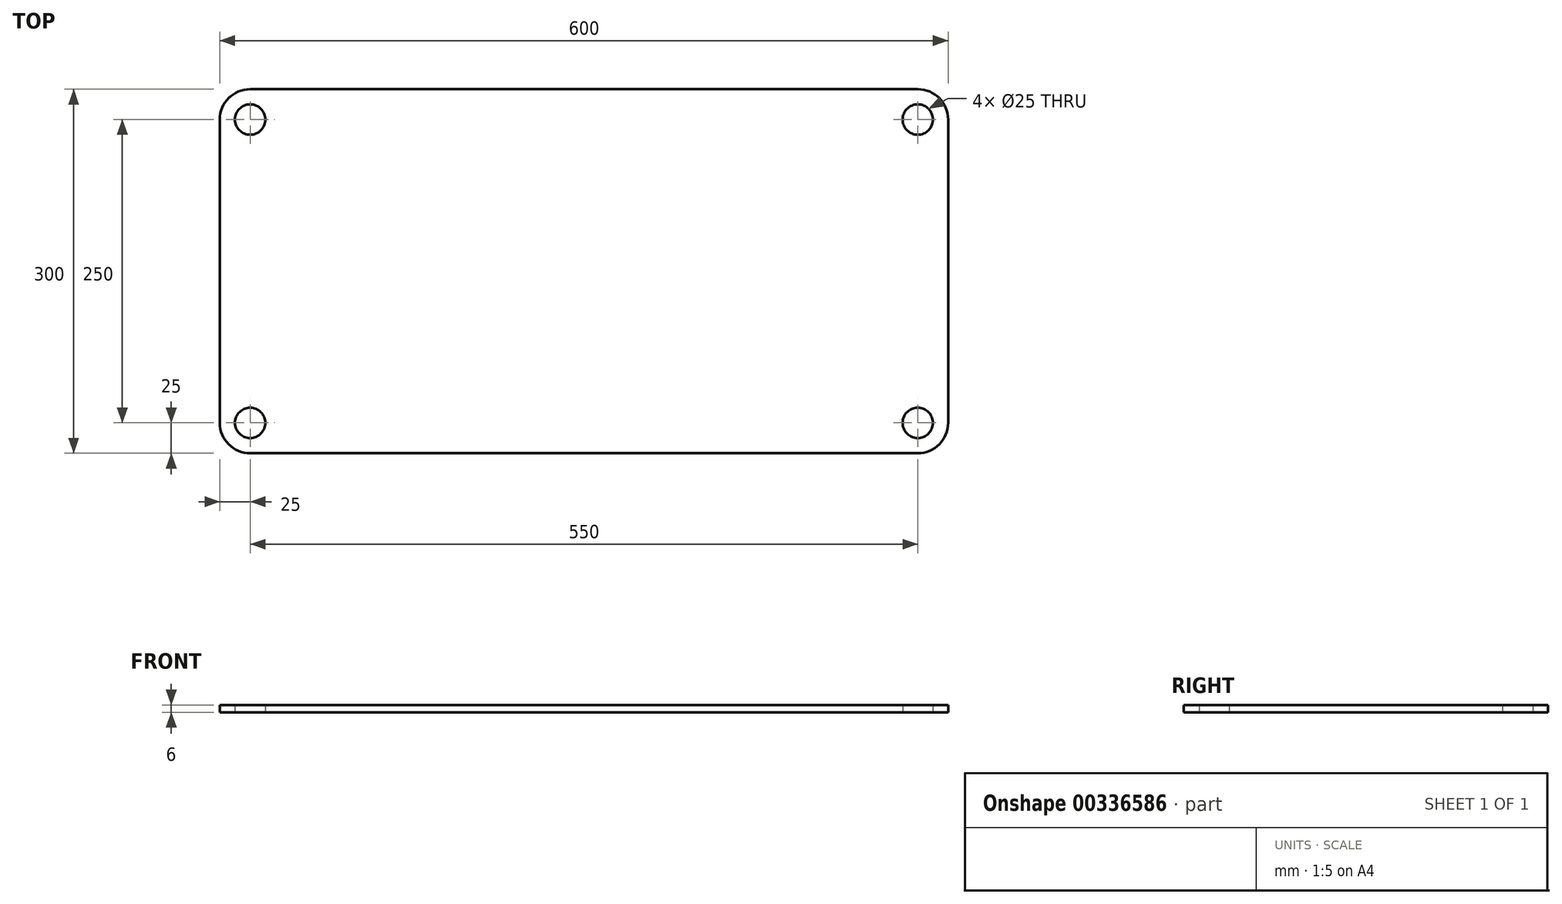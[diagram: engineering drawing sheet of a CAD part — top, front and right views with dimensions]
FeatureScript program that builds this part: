
annotation { "Feature Type Name" : "Feature", "Feature Type Description" : "" }
export const myFeature = defineFeature(function(context is Context, id is Id, definition is map)
    precondition{}
    {
        {
            var Q0;
            Q0=qCreatedBy(makeId("Top.planeOp"),FACE);
            var sketch = newSketch(context, id + "F0", { "sketchPlane" : qUnion([Q0])});
            skLineSegment(sketch, "E0.bottom", {"start": v(275, -150) * mm, "end": v(-275, -150) * mm});
            skLineSegment(sketch, "E0.top", {"start": v(275, 150) * mm, "end": v(-275, 150) * mm});
            skLineSegment(sketch, "E0.left", {"start": v(300, -125) * mm, "end": v(300, 125) * mm});
            skLineSegment(sketch, "E0.right", {"start": v(-300, -125) * mm, "end": v(-300, 125) * mm});
            skPoint(sketch, "E0.middle", {"position": v(0, 0) * mm});
            skPoint(sketch, "E1.visualSharp", {"position": v(-300, 150) * mm});
            skArc(sketch, "E1.filletArc", {"start": v(-275, 150) * mm, "mid": v(-292.68, 142.68) * mm, "end": v(-300, 125) * mm});
            skPoint(sketch, "E2.visualSharp", {"position": v(-300, -150) * mm});
            skArc(sketch, "E2.filletArc", {"start": v(-300, -125) * mm, "mid": v(-292.68, -142.68) * mm, "end": v(-275, -150) * mm});
            skPoint(sketch, "E3.visualSharp", {"position": v(300, 150) * mm});
            skArc(sketch, "E3.filletArc", {"start": v(300, 125) * mm, "mid": v(292.68, 142.68) * mm, "end": v(275, 150) * mm});
            skPoint(sketch, "E4.visualSharp", {"position": v(300, -150) * mm});
            skArc(sketch, "E4.filletArc", {"start": v(275, -150) * mm, "mid": v(292.68, -142.68) * mm, "end": v(300, -125) * mm});
            skSolve(sketch);
        }
        {
            var Q0;
            Q0=makeQuery(id+"F0.imprint","IMPRINT",FACE,{"disambiguationData":[TD([[makeQuery(id+"F0.imprint","IMPRINT",EDGE,{"derivedFrom":sQuery(id+"F0.wireOp",EDGE,"E0.bottom")}),-1.0]])]});
            extrude(context, id + "F1", {"entities" : qUnion([Q0]), "depth" : 6 * mm});
        }
        {
            var Q0;
            Q0=sQuery(id+"F0.wireOp",VERTEX,"E2.filletArc.center");
            var Q1;
            Q1=makeQuery(id+"F1.opExtrude","SWEPT_BODY",BODY,{"disambiguationData":[OSD([sQuery(id+"F0.wireOp",EDGE,"E0.bottom"),sQuery(id+"F0.wireOp",EDGE,"E0.top"),sQuery(id+"F0.wireOp",EDGE,"E0.left"),sQuery(id+"F0.wireOp",EDGE,"E0.right"),sQuery(id+"F0.wireOp",EDGE,"E1.filletArc"),sQuery(id+"F0.wireOp",EDGE,"E2.filletArc"),sQuery(id+"F0.wireOp",EDGE,"E3.filletArc"),sQuery(id+"F0.wireOp",EDGE,"E4.filletArc")])]});
            hole(context, id + "F2", {"style" : HoleStyle.SIMPLE, "endStyle" : HoleEndStyle.THROUGH, "oppositeDirection" : true, "holeDiameter" : 25 * mm, "tappedDepth" : 12 * mm, "tapClearance" : 3, "locations" : qUnion([Q0]), "scope" : qUnion([Q1])});
        }
        {
            var Q0;
            Q0=sQuery(id+"F0.wireOp",VERTEX,"E1.filletArc.center");
            var Q1;
            Q1=sQuery(id+"F0.wireOp",VERTEX,"E4.filletArc.center");
            var Q2;
            Q2=makeQuery(id+"F1.opExtrude","SWEPT_BODY",BODY,{"disambiguationData":[OSD([sQuery(id+"F0.wireOp",EDGE,"E0.bottom"),sQuery(id+"F0.wireOp",EDGE,"E0.top"),sQuery(id+"F0.wireOp",EDGE,"E0.left"),sQuery(id+"F0.wireOp",EDGE,"E0.right"),sQuery(id+"F0.wireOp",EDGE,"E1.filletArc"),sQuery(id+"F0.wireOp",EDGE,"E2.filletArc"),sQuery(id+"F0.wireOp",EDGE,"E3.filletArc"),sQuery(id+"F0.wireOp",EDGE,"E4.filletArc")])]});
            hole(context, id + "F3", {"style" : HoleStyle.SIMPLE, "endStyle" : HoleEndStyle.THROUGH, "oppositeDirection" : true, "holeDiameter" : 25 * mm, "tappedDepth" : 12 * mm, "tapClearance" : 3, "locations" : qUnion([Q0, Q1]), "scope" : qUnion([Q2])});
        }
        {
            var Q0;
            Q0=sQuery(id+"F0.wireOp",VERTEX,"E3.filletArc.center");
            var Q1;
            Q1=makeQuery(id+"F1.opExtrude","SWEPT_BODY",BODY,{"disambiguationData":[OSD([sQuery(id+"F0.wireOp",EDGE,"E0.bottom"),sQuery(id+"F0.wireOp",EDGE,"E0.top"),sQuery(id+"F0.wireOp",EDGE,"E0.left"),sQuery(id+"F0.wireOp",EDGE,"E0.right"),sQuery(id+"F0.wireOp",EDGE,"E1.filletArc"),sQuery(id+"F0.wireOp",EDGE,"E2.filletArc"),sQuery(id+"F0.wireOp",EDGE,"E3.filletArc"),sQuery(id+"F0.wireOp",EDGE,"E4.filletArc")])]});
            hole(context, id + "F4", {"style" : HoleStyle.SIMPLE, "endStyle" : HoleEndStyle.THROUGH, "oppositeDirection" : true, "holeDiameter" : 25 * mm, "tappedDepth" : 12 * mm, "tapClearance" : 3, "locations" : qUnion([Q0]), "scope" : qUnion([Q1])});
        }
    });
